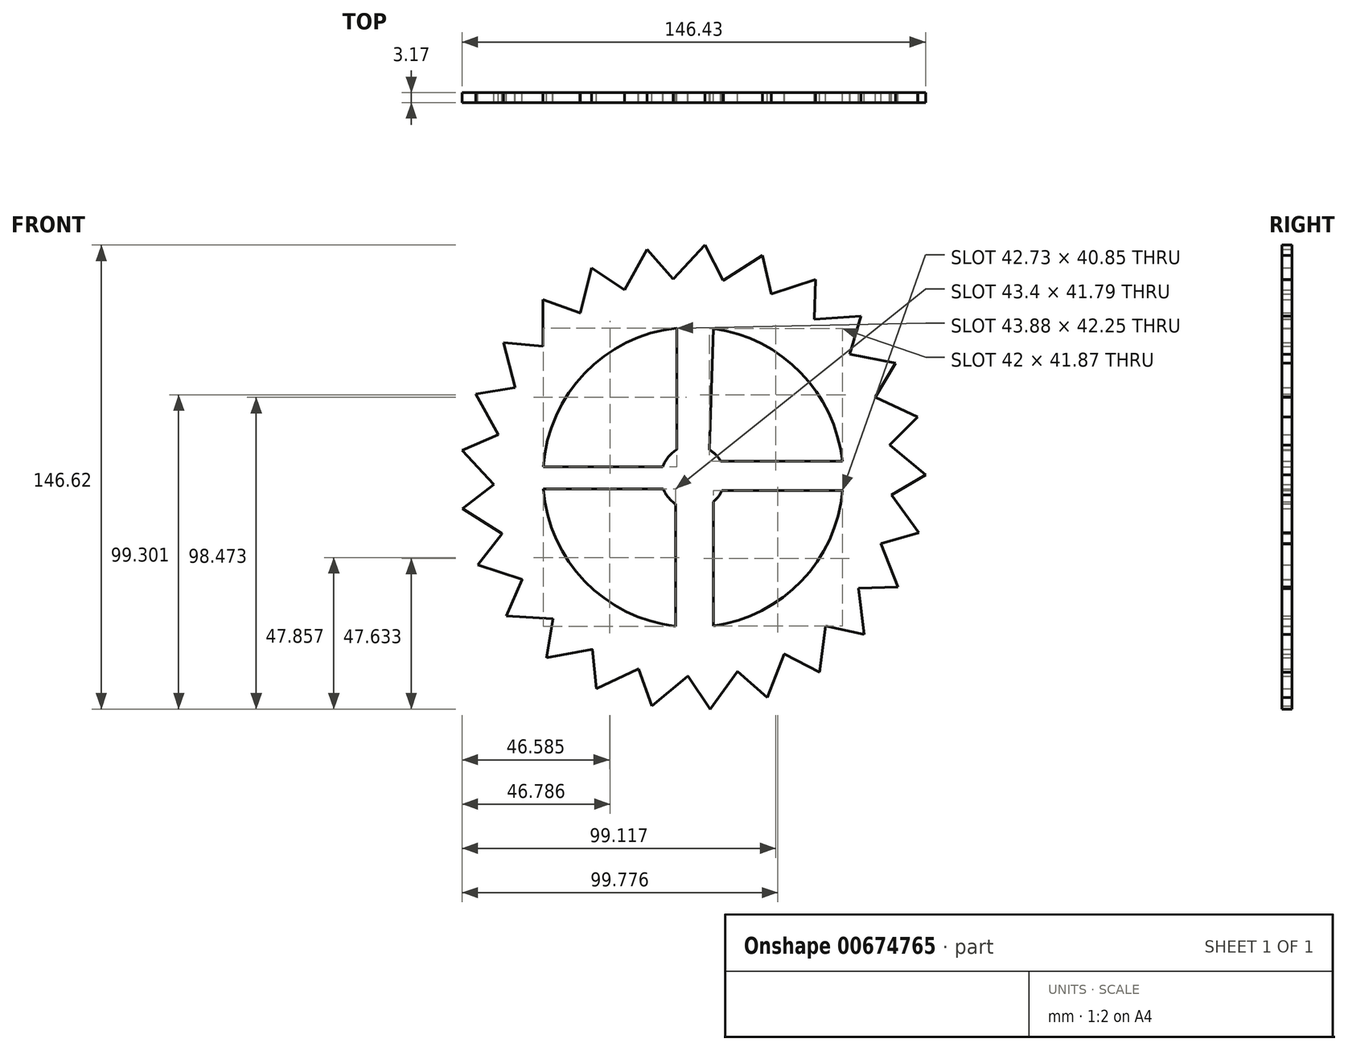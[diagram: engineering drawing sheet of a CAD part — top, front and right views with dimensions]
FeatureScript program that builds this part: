
annotation { "Feature Type Name" : "Feature", "Feature Type Description" : "" }
export const myFeature = defineFeature(function(context is Context, id is Id, definition is map)
    precondition{}
    {
        {
            var Q0;
            Q0=qCreatedBy(makeId("Front.planeOp"),FACE);
            var sketch = newSketch(context, id + "F0", { "sketchPlane" : qUnion([Q0])});
            skCircle(sketch, "E0", {"center": v(0, 0) * mm, "radius": 62.96 * mm});
            skLineSegment(sketch, "E1", {"start": v(-47.42, 41.41) * mm, "end": v(-47.42, 56.1) * mm});
            skLineSegment(sketch, "E2", {"start": v(-47.42, 56.1) * mm, "end": v(-35.68, 51.87) * mm});
            skLineSegment(sketch, "E3.1.0", {"start": v(-59.89, 42.55) * mm, "end": v(-47.46, 41.37) * mm});
            skLineSegment(sketch, "E3.1.1", {"start": v(-56.23, 28.32) * mm, "end": v(-59.89, 42.55) * mm});
            skLineSegment(sketch, "E3.2.0", {"start": v(-68.58, 26.32) * mm, "end": v(-56.26, 28.26) * mm});
            skLineSegment(sketch, "E3.2.1", {"start": v(-61.5, 13.44) * mm, "end": v(-68.58, 26.32) * mm});
            skLineSegment(sketch, "E3.3.0", {"start": v(-72.97, 8.43) * mm, "end": v(-61.52, 13.39) * mm});
            skLineSegment(sketch, "E3.3.1", {"start": v(-62.92, -2.28) * mm, "end": v(-72.97, 8.43) * mm});
            skLineSegment(sketch, "E3.4.0", {"start": v(-72.78, -9.98) * mm, "end": v(-62.92, -2.33) * mm});
            skLineSegment(sketch, "E3.4.1", {"start": v(-60.38, -17.85) * mm, "end": v(-72.78, -9.98) * mm});
            skLineSegment(sketch, "E3.5.0", {"start": v(-68.01, -27.77) * mm, "end": v(-60.36, -17.9) * mm});
            skLineSegment(sketch, "E3.5.1", {"start": v(-54.04, -32.3) * mm, "end": v(-68.01, -27.77) * mm});
            skLineSegment(sketch, "E3.6.0", {"start": v(-58.97, -43.8) * mm, "end": v(-54, -32.36) * mm});
            skLineSegment(sketch, "E3.6.1", {"start": v(-44.3, -44.73) * mm, "end": v(-58.97, -43.8) * mm});
            skLineSegment(sketch, "E3.7.0", {"start": v(-46.22, -57.1) * mm, "end": v(-44.27, -44.77) * mm});
            skLineSegment(sketch, "E3.7.1", {"start": v(-31.8, -54.34) * mm, "end": v(-46.22, -57.1) * mm});
            skLineSegment(sketch, "E3.8.0", {"start": v(-30.57, -66.8) * mm, "end": v(-31.74, -54.37) * mm});
            skLineSegment(sketch, "E3.8.1", {"start": v(-17.28, -60.54) * mm, "end": v(-30.57, -66.8) * mm});
            skLineSegment(sketch, "E3.9.0", {"start": v(-13, -72.3) * mm, "end": v(-17.22, -60.56) * mm});
            skLineSegment(sketch, "E3.9.1", {"start": v(-1.68, -62.94) * mm, "end": v(-13, -72.3) * mm});
            skLineSegment(sketch, "E3.10.0", {"start": v(5.4, -73.26) * mm, "end": v(-1.62, -62.94) * mm});
            skLineSegment(sketch, "E3.10.1", {"start": v(14.03, -61.38) * mm, "end": v(5.4, -73.26) * mm});
            skLineSegment(sketch, "E3.11.0", {"start": v(23.44, -69.62) * mm, "end": v(14.08, -61.36) * mm});
            skLineSegment(sketch, "E3.11.1", {"start": v(28.85, -55.96) * mm, "end": v(23.44, -69.62) * mm});
            skLineSegment(sketch, "E3.12.0", {"start": v(40.02, -61.6) * mm, "end": v(28.9, -55.93) * mm});
            skLineSegment(sketch, "E3.12.1", {"start": v(41.86, -47.03) * mm, "end": v(40.02, -61.6) * mm});
            skLineSegment(sketch, "E3.13.0", {"start": v(54.08, -49.72) * mm, "end": v(41.9, -46.99) * mm});
            skLineSegment(sketch, "E3.13.1", {"start": v(52.24, -35.14) * mm, "end": v(54.08, -49.72) * mm});
            skLineSegment(sketch, "E3.14.0", {"start": v(64.75, -34.7) * mm, "end": v(52.27, -35.1) * mm});
            skLineSegment(sketch, "E3.14.1", {"start": v(59.34, -21.05) * mm, "end": v(64.75, -34.7) * mm});
            skLineSegment(sketch, "E3.15.0", {"start": v(71.34, -17.51) * mm, "end": v(59.36, -21) * mm});
            skLineSegment(sketch, "E3.15.1", {"start": v(62.7, -5.63) * mm, "end": v(71.34, -17.51) * mm});
            skLineSegment(sketch, "E3.16.0", {"start": v(73.46, 0.78) * mm, "end": v(62.71, -5.57) * mm});
            skLineSegment(sketch, "E3.16.1", {"start": v(62.14, 10.14) * mm, "end": v(73.46, 0.78) * mm});
            skLineSegment(sketch, "E3.17.0", {"start": v(70.95, 19.02) * mm, "end": v(62.13, 10.2) * mm});
            skLineSegment(sketch, "E3.17.1", {"start": v(57.66, 25.28) * mm, "end": v(70.95, 19.02) * mm});
            skLineSegment(sketch, "E3.18.0", {"start": v(64, 36.07) * mm, "end": v(57.64, 25.33) * mm});
            skLineSegment(sketch, "E3.18.1", {"start": v(49.56, 38.82) * mm, "end": v(64, 36.07) * mm});
            skLineSegment(sketch, "E3.19.0", {"start": v(53.01, 50.85) * mm, "end": v(49.53, 38.87) * mm});
            skLineSegment(sketch, "E3.19.1", {"start": v(38.35, 49.93) * mm, "end": v(53.01, 50.85) * mm});
            skLineSegment(sketch, "E3.20.0", {"start": v(38.7, 62.44) * mm, "end": v(38.3, 49.97) * mm});
            skLineSegment(sketch, "E3.20.1", {"start": v(24.73, 57.9) * mm, "end": v(38.7, 62.44) * mm});
            skLineSegment(sketch, "E3.21.0", {"start": v(21.96, 70.1) * mm, "end": v(24.68, 57.92) * mm});
            skLineSegment(sketch, "E3.21.1", {"start": v(9.55, 62.23) * mm, "end": v(21.96, 70.1) * mm});
            skLineSegment(sketch, "E3.22.0", {"start": v(3.83, 73.36) * mm, "end": v(9.5, 62.24) * mm});
            skLineSegment(sketch, "E3.22.1", {"start": v(-6.22, 62.65) * mm, "end": v(3.83, 73.36) * mm});
            skLineSegment(sketch, "E3.23.0", {"start": v(-14.53, 72) * mm, "end": v(-6.28, 62.65) * mm});
            skLineSegment(sketch, "E3.23.1", {"start": v(-21.6, 59.14) * mm, "end": v(-14.53, 72) * mm});
            skLineSegment(sketch, "E3.24.0", {"start": v(-31.98, 66.13) * mm, "end": v(-21.66, 59.12) * mm});
            skLineSegment(sketch, "E3.24.1", {"start": v(-35.64, 51.9) * mm, "end": v(-31.98, 66.13) * mm});
            skCircle(sketch, "E4", {"center": v(0, 0) * mm, "radius": 10.08 * mm});
            skCircle(sketch, "E5", {"center": v(0, 0) * mm, "radius": 47.42 * mm});
            skLineSegment(sketch, "E6", {"start": v(-5.06, 8.72) * mm, "end": v(-5.06, 47.15) * mm});
            skLineSegment(sketch, "E7", {"start": v(5.15, 8.67) * mm, "end": v(6.48, 46.98) * mm});
            skLineSegment(sketch, "E8", {"start": v(-5.5, -8.46) * mm, "end": v(-5.5, -47.1) * mm});
            skLineSegment(sketch, "E9", {"start": v(6.38, -7.8) * mm, "end": v(6.38, -47) * mm});
            skLineSegment(sketch, "E10", {"start": v(8.7, 5.1) * mm, "end": v(47.15, 5.1) * mm});
            skLineSegment(sketch, "E11", {"start": v(47.15, 5.1) * mm, "end": v(46.17, 7.07) * mm});
            skLineSegment(sketch, "E12", {"start": v(9.14, -4.26) * mm, "end": v(47.23, -4.26) * mm});
            skLineSegment(sketch, "E13", {"start": v(-9.54, 3.27) * mm, "end": v(-47.31, 3.27) * mm});
            skLineSegment(sketch, "E14", {"start": v(-9.38, -3.7) * mm, "end": v(-47.28, -3.7) * mm});
            skSolve(sketch);
        }
        {
            var Q0;
            Q0 = qSketchRegion(id + "F0", true);
            var Q1;
            {var subQ0=sQuery(id+"F0.wireOp",EDGE,"E6");Q1=makeQuery(id+"F0.imprint","IMPRINT",FACE,{"disambiguationData":[TD([[makeQuery(id+"F0.imprint","IMPRINT",EDGE,{"derivedFrom":subQ0}),-1.0]])]});}
            var Q2;
            {var subQ0=sQuery(id+"F0.wireOp",EDGE,"E8");Q2=makeQuery(id+"F0.imprint","IMPRINT",FACE,{"disambiguationData":[TD([[makeQuery(id+"F0.imprint","IMPRINT",EDGE,{"derivedFrom":subQ0}),1.0]])]});}
            var Q3;
            {var subQ0=sQuery(id+"F0.wireOp",EDGE,"E10");Q3=makeQuery(id+"F0.imprint","IMPRINT",FACE,{"disambiguationData":[TD([[makeQuery(id+"F0.imprint","IMPRINT",EDGE,{"derivedFrom":subQ0}),-1.0]])]});}
            var Q4;
            {var subQ0=sQuery(id+"F0.wireOp",EDGE,"E13");Q4=makeQuery(id+"F0.imprint","IMPRINT",FACE,{"disambiguationData":[TD([[makeQuery(id+"F0.imprint","IMPRINT",EDGE,{"derivedFrom":subQ0}),1.0]])]});}
            var Q5;
            {var subQ0=sQuery(id+"F0.wireOp",EDGE,"E4");var subQ4=makeQuery(id+"F0.imprint","INTERSECT",VERTEX,{"derivedFrom":[subQ0,sQuery(id+"F0.wireOp",EDGE,"E7")]});Q5=makeQuery(id+"F0.imprint","IMPRINT",FACE,{"disambiguationData":[TD([[makeQuery(id+"F0.imprint","IMPRINT",EDGE,{"disambiguationData":[TD([[subQ4,1.0]])],"derivedFrom":subQ0}),1.0]])]});}
            extrude(context, id + "F1", {"entities" : qUnion([Q0, Q1, Q2, Q3, Q4, Q5]), "depth" : 3.17 * mm, "offsetDistance" : 25.4 * mm});
        }
    });
